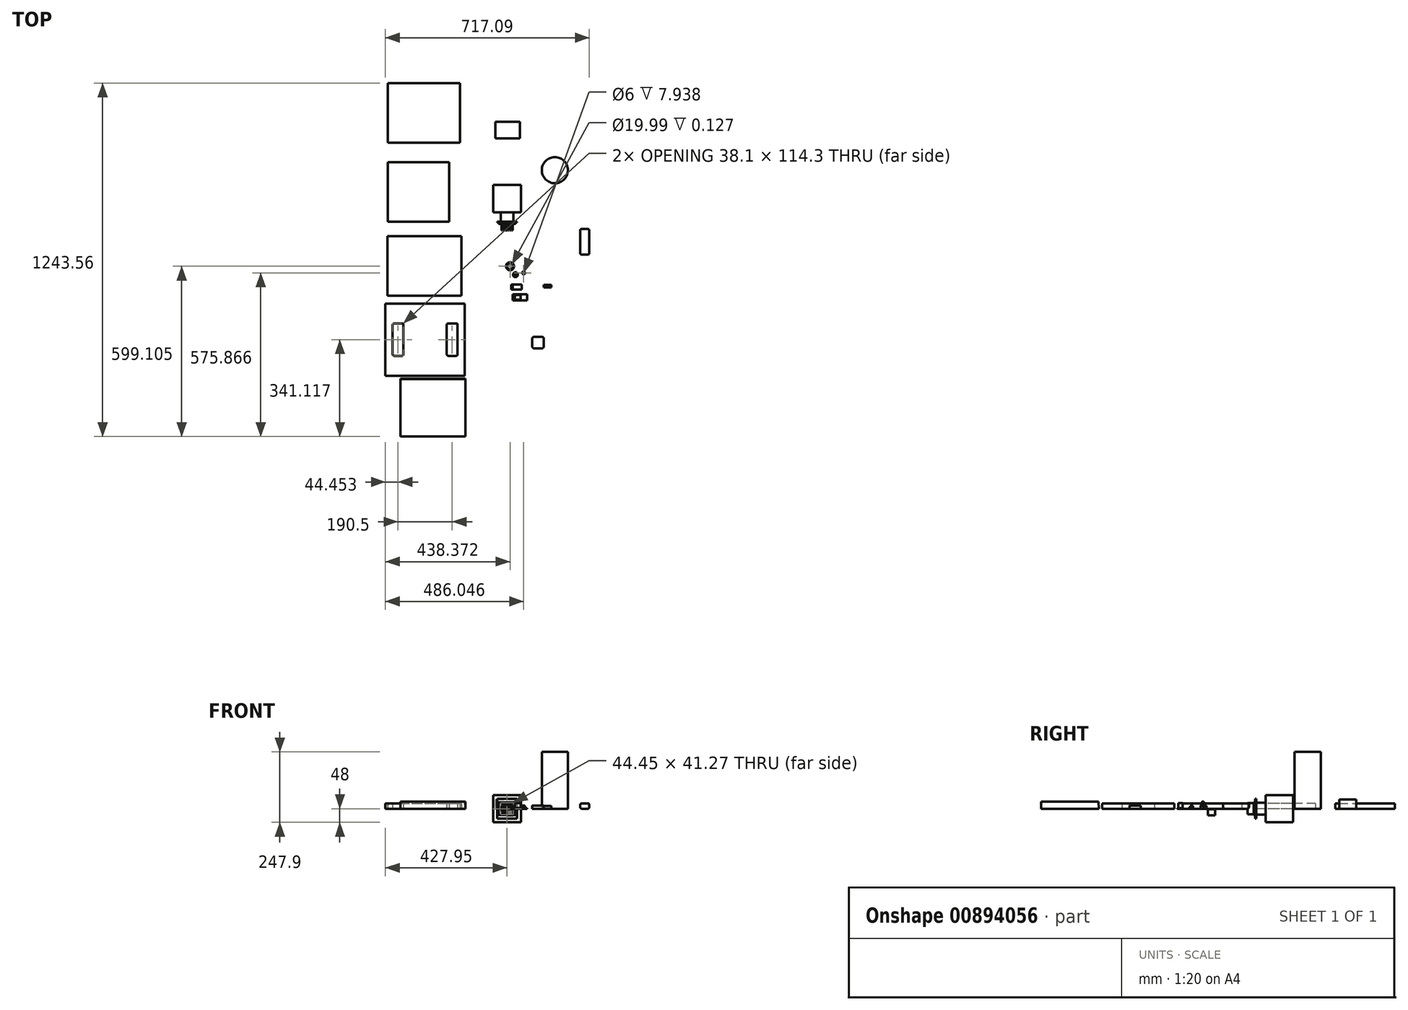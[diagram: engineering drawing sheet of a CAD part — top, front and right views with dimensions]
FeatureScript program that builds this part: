
annotation { "Feature Type Name" : "Feature", "Feature Type Description" : "" }
export const myFeature = defineFeature(function(context is Context, id is Id, definition is map)
    precondition{}
    {
        {
            var Q0;
            Q0=qCreatedBy(makeId("Front.planeOp"),FACE);
            var sketch = newSketch(context, id + "F0", { "sketchPlane" : qUnion([Q0])});
            skLineSegment(sketch, "E0.bottom", {"start": v(49, 48) * mm, "end": v(-49, 48) * mm});
            skLineSegment(sketch, "E0.top", {"start": v(49, -48) * mm, "end": v(-49, -48) * mm});
            skLineSegment(sketch, "E0.left", {"start": v(49, 48) * mm, "end": v(49, -48) * mm});
            skLineSegment(sketch, "E0.right", {"start": v(-49, 48) * mm, "end": v(-49, -48) * mm});
            skPoint(sketch, "E0.middle", {"position": v(0, 0) * mm});
            skSolve(sketch);
        }
        {
            var Q0;
            Q0 = qSketchRegion(id + "F0", true);
            extrude(context, id + "F1", {"entities" : qUnion([Q0]), "endBound" : BoundingType.SYMMETRIC, "depth" : 96.52 * mm, "offsetDistance" : 25.4 * mm});
        }
        {
            var Q0;
            Q0=qCreatedBy(makeId("Top.planeOp"),FACE);
            var sketch = newSketch(context, id + "F2", { "sketchPlane" : qUnion([Q0])});
            skLineSegment(sketch, "E1.bottom", {"start": v(-41.13, 211.34) * mm, "end": v(44.87, 211.34) * mm});
            skLineSegment(sketch, "E1.top", {"start": v(-41.13, 270.34) * mm, "end": v(44.87, 270.34) * mm});
            skLineSegment(sketch, "E1.left", {"start": v(-41.13, 211.34) * mm, "end": v(-41.13, 270.34) * mm});
            skLineSegment(sketch, "E1.right", {"start": v(44.87, 211.34) * mm, "end": v(44.87, 270.34) * mm});
            skSolve(sketch);
        }
        {
            var Q0;
            Q0 = qSketchRegion(id + "F2", true);
            extrude(context, id + "F3", {"entities" : qUnion([Q0]), "depth" : 33 * mm, "offsetDistance" : 25.4 * mm});
        }
        {
            var Q0;
            Q0=qCreatedBy(makeId("Top.planeOp"),FACE);
            var sketch = newSketch(context, id + "F4", { "sketchPlane" : qUnion([Q0])});
            skLineSegment(sketch, "E2.bottom", {"start": v(-419.23, 127.47) * mm, "end": v(-203.33, 127.47) * mm});
            skLineSegment(sketch, "E2.top", {"start": v(-419.23, -82.08) * mm, "end": v(-203.33, -82.08) * mm});
            skLineSegment(sketch, "E2.left", {"start": v(-419.23, 127.47) * mm, "end": v(-419.23, -82.08) * mm});
            skLineSegment(sketch, "E2.right", {"start": v(-203.33, 127.47) * mm, "end": v(-203.33, -82.08) * mm});
            skLineSegment(sketch, "E3.bottom", {"start": v(-420.68, -132.1) * mm, "end": v(-160.33, -132.1) * mm});
            skLineSegment(sketch, "E3.top", {"start": v(-420.68, -341.65) * mm, "end": v(-160.33, -341.65) * mm});
            skLineSegment(sketch, "E3.left", {"start": v(-420.68, -132.1) * mm, "end": v(-420.68, -341.65) * mm});
            skLineSegment(sketch, "E3.right", {"start": v(-160.33, -132.1) * mm, "end": v(-160.33, -341.65) * mm});
            skLineSegment(sketch, "E4.bottom", {"start": v(-427.95, -369.22) * mm, "end": v(-148.55, -369.22) * mm});
            skLineSegment(sketch, "E4.top", {"start": v(-427.95, -623.22) * mm, "end": v(-148.55, -623.22) * mm});
            skLineSegment(sketch, "E4.left", {"start": v(-427.95, -369.22) * mm, "end": v(-427.95, -623.22) * mm});
            skLineSegment(sketch, "E4.right", {"start": v(-148.55, -369.22) * mm, "end": v(-148.55, -623.22) * mm});
            skLineSegment(sketch, "E5.bottom", {"start": v(-212.05, -439.07) * mm, "end": v(-173.95, -439.07) * mm});
            skLineSegment(sketch, "E5.top", {"start": v(-212.05, -553.37) * mm, "end": v(-173.95, -553.37) * mm});
            skLineSegment(sketch, "E5.left", {"start": v(-212.05, -439.07) * mm, "end": v(-212.05, -553.37) * mm});
            skLineSegment(sketch, "E5.right", {"start": v(-173.95, -439.07) * mm, "end": v(-173.95, -553.37) * mm});
            skLineSegment(sketch, "E6", {"start": v(-427.95, -496.22) * mm, "end": v(-148.55, -496.22) * mm, "construction": true});
            skPoint(sketch, "E7", {"position": v(-173.95, -496.22) * mm});
            skLineSegment(sketch, "E8.bottom", {"start": v(-364.45, -439.07) * mm, "end": v(-402.55, -439.07) * mm});
            skLineSegment(sketch, "E8.top", {"start": v(-364.45, -553.37) * mm, "end": v(-402.55, -553.37) * mm});
            skLineSegment(sketch, "E8.left", {"start": v(-364.45, -439.07) * mm, "end": v(-364.45, -553.37) * mm});
            skLineSegment(sketch, "E8.right", {"start": v(-402.55, -439.07) * mm, "end": v(-402.55, -553.37) * mm});
            skPoint(sketch, "E8.middle", {"position": v(-383.5, -496.22) * mm});
            skLineSegment(sketch, "E9.bottom", {"start": v(-419.23, 196.67) * mm, "end": v(-165.23, 196.67) * mm});
            skLineSegment(sketch, "E9.top", {"start": v(-419.23, 406.22) * mm, "end": v(-165.23, 406.22) * mm});
            skLineSegment(sketch, "E9.left", {"start": v(-419.23, 196.67) * mm, "end": v(-419.23, 406.22) * mm});
            skLineSegment(sketch, "E9.right", {"start": v(-165.23, 196.67) * mm, "end": v(-165.23, 406.22) * mm});
            skSolve(sketch);
        }
        {
            var Q0;
            Q0=qCreatedBy(makeId("Top.planeOp"),FACE);
            var sketch = newSketch(context, id + "F5", { "sketchPlane" : qUnion([Q0])});
            skCircle(sketch, "E10", {"center": v(168.13, 99.9) * mm, "radius": 45.97 * mm});
            skSolve(sketch);
        }
        {
            var Q0;
            Q0 = qSketchRegion(id + "F5", true);
            extrude(context, id + "F6", {"entities" : qUnion([Q0]), "depth" : 199.9 * mm, "offsetDistance" : 25.4 * mm});
        }
        {
            var Q0;
            Q0=makeQuery(id+"F4.imprint","IMPRINT",FACE,{"disambiguationData":[TD([[makeQuery(id+"F4.imprint","IMPRINT",EDGE,{"derivedFrom":sQuery(id+"F4.wireOp",EDGE,"E4.bottom")}),-1.0]])]});
            var Q1;
            Q1=makeQuery(id+"F4.imprint","IMPRINT",FACE,{"disambiguationData":[TD([[makeQuery(id+"F4.imprint","IMPRINT",EDGE,{"derivedFrom":sQuery(id+"F4.wireOp",EDGE,"E3.bottom")}),-1.0]])]});
            var Q2;
            Q2=makeQuery(id+"F4.imprint","IMPRINT",FACE,{"disambiguationData":[TD([[makeQuery(id+"F4.imprint","IMPRINT",EDGE,{"derivedFrom":sQuery(id+"F4.wireOp",EDGE,"E2.bottom")}),-1.0]])]});
            var Q3;
            Q3=makeQuery(id+"F4.imprint","IMPRINT",FACE,{"disambiguationData":[TD([[makeQuery(id+"F4.imprint","IMPRINT",EDGE,{"derivedFrom":sQuery(id+"F4.wireOp",EDGE,"E9.bottom")}),1.0]])]});
            extrude(context, id + "F7", {"entities" : qUnion([Q0, Q1, Q2, Q3]), "depth" : 19.05 * mm, "offsetDistance" : 25.4 * mm});
        }
        {
            var Q0;
            Q0=makeQuery(id+"F1.opExtrude","CAP_FACE",FACE,{"disambiguationData":[OSD([sQuery(id+"F0.wireOp",EDGE,"E0.bottom"),sQuery(id+"F0.wireOp",EDGE,"E0.top"),sQuery(id+"F0.wireOp",EDGE,"E0.left"),sQuery(id+"F0.wireOp",EDGE,"E0.right")])],"isStart":false});
            var sketch = newSketch(context, id + "F8", { "sketchPlane" : qUnion([Q0])});
            skLineSegment(sketch, "E11.bottom", {"start": v(22.23, 20.64) * mm, "end": v(-22.23, 20.64) * mm});
            skLineSegment(sketch, "E11.top", {"start": v(22.22, -20.64) * mm, "end": v(-22.22, -20.64) * mm});
            skLineSegment(sketch, "E11.left", {"start": v(22.23, 20.64) * mm, "end": v(22.23, -20.64) * mm});
            skLineSegment(sketch, "E11.right", {"start": v(-22.23, 20.64) * mm, "end": v(-22.23, -20.64) * mm});
            skPoint(sketch, "E11.middle", {"position": v(0, 0) * mm});
            skSolve(sketch);
        }
        {
            var Q0;
            Q0 = qSketchRegion(id + "F8", true);
            extrude(context, id + "F9", {"entities" : qUnion([Q0]), "operationType" : NewBodyOperationType.ADD, "depth" : 33.02 * mm, "offsetDistance" : 25.4 * mm});
        }
        {
            var Q0;
            Q0=makeQuery(id+"F9.opExtrude","CAP_FACE",FACE,{"disambiguationData":[OSD([sQuery(id+"F8.wireOp",EDGE,"E11.bottom"),sQuery(id+"F8.wireOp",EDGE,"E11.top"),sQuery(id+"F8.wireOp",EDGE,"E11.left"),sQuery(id+"F8.wireOp",EDGE,"E11.right")])],"isStart":false});
            var sketch = newSketch(context, id + "F10", { "sketchPlane" : qUnion([Q0])});
            skLineSegment(sketch, "E12.bottom", {"start": v(34.92, 34.93) * mm, "end": v(-34.93, 34.93) * mm});
            skLineSegment(sketch, "E12.top", {"start": v(34.93, -34.93) * mm, "end": v(-34.92, -34.93) * mm});
            skLineSegment(sketch, "E12.left", {"start": v(34.92, 34.93) * mm, "end": v(34.93, -34.93) * mm});
            skLineSegment(sketch, "E12.right", {"start": v(-34.93, 34.93) * mm, "end": v(-34.92, -34.93) * mm});
            skPoint(sketch, "E12.middle", {"position": v(0, 0) * mm});
            skSolve(sketch);
        }
        {
            var Q0;
            Q0 = qSketchRegion(id + "F10", true);
            extrude(context, id + "F11", {"entities" : qUnion([Q0]), "operationType" : NewBodyOperationType.ADD, "depth" : 3.3 * mm, "offsetDistance" : 25.4 * mm});
        }
        {
            var Q0;
            Q0=makeQuery(id+"F11.opExtrude","CAP_FACE",FACE,{"disambiguationData":[OSD([sQuery(id+"F10.wireOp",EDGE,"E12.bottom"),sQuery(id+"F10.wireOp",EDGE,"E12.top"),sQuery(id+"F10.wireOp",EDGE,"E12.left"),sQuery(id+"F10.wireOp",EDGE,"E12.right")])],"isStart":false});
            var sketch = newSketch(context, id + "F12", { "sketchPlane" : qUnion([Q0])});
            skLineSegment(sketch, "E13.bottom", {"start": v(30.23, 22.5) * mm, "end": v(-30.23, 22.5) * mm});
            skLineSegment(sketch, "E13.top", {"start": v(30.23, -22.5) * mm, "end": v(-30.23, -22.5) * mm});
            skLineSegment(sketch, "E13.left", {"start": v(30.23, 22.5) * mm, "end": v(30.23, -22.5) * mm});
            skLineSegment(sketch, "E13.right", {"start": v(-30.23, 22.5) * mm, "end": v(-30.23, -22.5) * mm});
            skPoint(sketch, "E13.middle", {"position": v(0, 0) * mm});
            skSolve(sketch);
        }
        {
            var Q0;
            Q0 = qSketchRegion(id + "F12", true);
            extrude(context, id + "F13", {"entities" : qUnion([Q0]), "operationType" : NewBodyOperationType.ADD, "depth" : 4.76 * mm, "offsetDistance" : 25.4 * mm});
        }
        {
            var Q0;
            Q0=makeQuery(id+"F13.opExtrude","CAP_FACE",FACE,{"disambiguationData":[OSD([sQuery(id+"F12.wireOp",EDGE,"E13.bottom"),sQuery(id+"F12.wireOp",EDGE,"E13.top"),sQuery(id+"F12.wireOp",EDGE,"E13.left"),sQuery(id+"F12.wireOp",EDGE,"E13.right")])],"isStart":false});
            var sketch = newSketch(context, id + "F14", { "sketchPlane" : qUnion([Q0])});
            skLineSegment(sketch, "E14.bottom", {"start": v(19.84, 19.84) * mm, "end": v(-19.84, 19.84) * mm});
            skLineSegment(sketch, "E14.top", {"start": v(19.84, -19.84) * mm, "end": v(-19.84, -19.84) * mm});
            skLineSegment(sketch, "E14.left", {"start": v(19.84, 19.84) * mm, "end": v(19.84, -19.84) * mm});
            skLineSegment(sketch, "E14.right", {"start": v(-19.84, 19.84) * mm, "end": v(-19.84, -19.84) * mm});
            skPoint(sketch, "E14.middle", {"position": v(0, 0) * mm});
            skLineSegment(sketch, "E15", {"start": v(-17.3, 19.84) * mm, "end": v(-17.3, -19.84) * mm});
            skLineSegment(sketch, "E16.1.0.0", {"start": v(-15.02, 19.84) * mm, "end": v(-15.02, -19.84) * mm});
            skLineSegment(sketch, "E16.2.0.0", {"start": v(-12.73, 19.84) * mm, "end": v(-12.73, -19.84) * mm});
            skLineSegment(sketch, "E16.3.0.0", {"start": v(-10.45, 19.84) * mm, "end": v(-10.45, -19.84) * mm});
            skLineSegment(sketch, "E16.4.0.0", {"start": v(-8.16, 19.84) * mm, "end": v(-8.16, -19.84) * mm});
            skLineSegment(sketch, "E16.5.0.0", {"start": v(-5.87, 19.84) * mm, "end": v(-5.87, -19.84) * mm});
            skLineSegment(sketch, "E16.6.0.0", {"start": v(-3.59, 19.84) * mm, "end": v(-3.59, -19.84) * mm});
            skLineSegment(sketch, "E16.7.0.0", {"start": v(-1.3, 19.84) * mm, "end": v(-1.3, -19.84) * mm});
            skLineSegment(sketch, "E16.8.0.0", {"start": v(0.98, 19.84) * mm, "end": v(0.98, -19.84) * mm});
            skLineSegment(sketch, "E16.9.0.0", {"start": v(3.27, 19.84) * mm, "end": v(3.27, -19.84) * mm});
            skLineSegment(sketch, "E16.10.0.0", {"start": v(5.56, 19.84) * mm, "end": v(5.56, -19.84) * mm});
            skLineSegment(sketch, "E16.11.0.0", {"start": v(7.84, 19.84) * mm, "end": v(7.84, -19.84) * mm});
            skLineSegment(sketch, "E16.12.0.0", {"start": v(10.13, 19.84) * mm, "end": v(10.13, -19.84) * mm});
            skLineSegment(sketch, "E16.13.0.0", {"start": v(12.41, 19.84) * mm, "end": v(12.41, -19.84) * mm});
            skLineSegment(sketch, "E16.14.0.0", {"start": v(14.7, 19.84) * mm, "end": v(14.7, -19.84) * mm});
            skLineSegment(sketch, "E16.direction1", {"start": v(-17.3, -19.84) * mm, "end": v(-15.02, -19.84) * mm, "construction": true});
            skLineSegment(sketch, "E17.0.15.0", {"start": v(16.99, 19.84) * mm, "end": v(16.99, -19.84) * mm});
            skSolve(sketch);
        }
        {
            var Q0;
            {var subQ0=sQuery(id+"F14.wireOp",EDGE,"E14.right");Q0=makeQuery(id+"F14.imprint","IMPRINT",FACE,{"disambiguationData":[TD([[makeQuery(id+"F14.imprint","IMPRINT",EDGE,{"derivedFrom":subQ0}),1.0]])]});}
            var Q1;
            {var subQ0=sQuery(id+"F14.wireOp",EDGE,"E16.1.0.0");Q1=makeQuery(id+"F14.imprint","IMPRINT",FACE,{"disambiguationData":[TD([[makeQuery(id+"F14.imprint","IMPRINT",EDGE,{"derivedFrom":subQ0}),1.0]])]});}
            var Q2;
            {var subQ0=sQuery(id+"F14.wireOp",EDGE,"E16.3.0.0");Q2=makeQuery(id+"F14.imprint","IMPRINT",FACE,{"disambiguationData":[TD([[makeQuery(id+"F14.imprint","IMPRINT",EDGE,{"derivedFrom":subQ0}),1.0]])]});}
            var Q3;
            {var subQ0=sQuery(id+"F14.wireOp",EDGE,"E16.5.0.0");Q3=makeQuery(id+"F14.imprint","IMPRINT",FACE,{"disambiguationData":[TD([[makeQuery(id+"F14.imprint","IMPRINT",EDGE,{"derivedFrom":subQ0}),1.0]])]});}
            var Q4;
            {var subQ0=sQuery(id+"F14.wireOp",EDGE,"E16.7.0.0");Q4=makeQuery(id+"F14.imprint","IMPRINT",FACE,{"disambiguationData":[TD([[makeQuery(id+"F14.imprint","IMPRINT",EDGE,{"derivedFrom":subQ0}),1.0]])]});}
            var Q5;
            {var subQ0=sQuery(id+"F14.wireOp",EDGE,"E16.9.0.0");Q5=makeQuery(id+"F14.imprint","IMPRINT",FACE,{"disambiguationData":[TD([[makeQuery(id+"F14.imprint","IMPRINT",EDGE,{"derivedFrom":subQ0}),1.0]])]});}
            var Q6;
            {var subQ0=sQuery(id+"F14.wireOp",EDGE,"E16.11.0.0");Q6=makeQuery(id+"F14.imprint","IMPRINT",FACE,{"disambiguationData":[TD([[makeQuery(id+"F14.imprint","IMPRINT",EDGE,{"derivedFrom":subQ0}),1.0]])]});}
            var Q7;
            {var subQ0=sQuery(id+"F14.wireOp",EDGE,"E16.13.0.0");Q7=makeQuery(id+"F14.imprint","IMPRINT",FACE,{"disambiguationData":[TD([[makeQuery(id+"F14.imprint","IMPRINT",EDGE,{"derivedFrom":subQ0}),1.0]])]});}
            var Q8;
            {var subQ0=sQuery(id+"F14.wireOp",EDGE,"E14.left");Q8=makeQuery(id+"F14.imprint","IMPRINT",FACE,{"disambiguationData":[TD([[makeQuery(id+"F14.imprint","IMPRINT",EDGE,{"derivedFrom":subQ0}),-1.0]])]});}
            extrude(context, id + "F15", {"entities" : qUnion([Q0, Q1, Q2, Q3, Q4, Q5, Q6, Q7, Q8]), "operationType" : NewBodyOperationType.ADD, "depth" : 22.22 * mm, "offsetDistance" : 25.4 * mm});
        }
        {
            var Q0;
            Q0=qCreatedBy(makeId("Top.planeOp"),FACE);
            var sketch = newSketch(context, id + "F16", { "sketchPlane" : qUnion([Q0])});
            skLineSegment(sketch, "E18.bottom", {"start": v(257.4, -106.84) * mm, "end": v(289.14, -106.84) * mm});
            skLineSegment(sketch, "E18.top", {"start": v(257.4, -197.32) * mm, "end": v(289.14, -197.32) * mm});
            skLineSegment(sketch, "E18.left", {"start": v(257.4, -106.84) * mm, "end": v(257.4, -197.32) * mm});
            skLineSegment(sketch, "E18.right", {"start": v(289.14, -106.84) * mm, "end": v(289.14, -197.32) * mm});
            skSolve(sketch);
        }
        {
            var Q0;
            Q0 = qSketchRegion(id + "F16", true);
            extrude(context, id + "F17", {"entities" : qUnion([Q0]), "depth" : 19.05 * mm, "offsetDistance" : 25.4 * mm});
        }
        {
            var Q0;
            Q0=makeQuery(id+"F17.opExtrude","CAP_FACE",FACE,{"disambiguationData":[OSD([sQuery(id+"F16.wireOp",EDGE,"E18.bottom"),sQuery(id+"F16.wireOp",EDGE,"E18.top"),sQuery(id+"F16.wireOp",EDGE,"E18.left"),sQuery(id+"F16.wireOp",EDGE,"E18.right")])],"isStart":false});
            var Q1;
            Q1=makeQuery(id+"F17.opExtrude","SWEPT_FACE",FACE,{"disambiguationData":[OSD([sQuery(id+"F16.wireOp",EDGE,"E18.top")])]});
            var Q2;
            Q2=makeQuery(id+"F17.opExtrude","SWEPT_FACE",FACE,{"disambiguationData":[OSD([sQuery(id+"F16.wireOp",EDGE,"E18.bottom")])]});
            var Q3;
            Q3=makeQuery(id+"F17.opExtrude","CAP_FACE",FACE,{"disambiguationData":[OSD([sQuery(id+"F16.wireOp",EDGE,"E18.bottom"),sQuery(id+"F16.wireOp",EDGE,"E18.top"),sQuery(id+"F16.wireOp",EDGE,"E18.left"),sQuery(id+"F16.wireOp",EDGE,"E18.right")])],"isStart":true});
            fillet(context, id + "F18", {"entities" : qUnion([Q0, Q1, Q2, Q3]), "radius" : 5.08 * mm, "tangentPropagation" : true, "allowEdgeOverflow" : false});
        }
        {
            var Q0;
            Q0=qCreatedBy(makeId("Top.planeOp"),FACE);
            var sketch = newSketch(context, id + "F19", { "sketchPlane" : qUnion([Q0])});
            skLineSegment(sketch, "E19.bottom", {"start": v(-374.6, -634.14) * mm, "end": v(-146, -634.14) * mm});
            skLineSegment(sketch, "E19.top", {"start": v(-374.6, -837.34) * mm, "end": v(-146, -837.34) * mm});
            skLineSegment(sketch, "E19.left", {"start": v(-374.6, -634.14) * mm, "end": v(-374.6, -837.34) * mm});
            skLineSegment(sketch, "E19.right", {"start": v(-146, -634.14) * mm, "end": v(-146, -837.34) * mm});
            skSolve(sketch);
        }
        {
            var Q0;
            Q0=makeQuery(id+"F19.imprint","IMPRINT",FACE,{"disambiguationData":[TD([[makeQuery(id+"F19.imprint","IMPRINT",EDGE,{"derivedFrom":sQuery(id+"F19.wireOp",EDGE,"E19.bottom")}),-1.0]])]});
            extrude(context, id + "F20", {"entities" : qUnion([Q0]), "depth" : 25.4 * mm, "offsetDistance" : 25.4 * mm});
        }
        {
            var Q0;
            Q0=makeQuery(id+"F20.opExtrude","SWEPT_FACE",FACE,{"disambiguationData":[OSD([sQuery(id+"F19.wireOp",EDGE,"E19.left")])]});
            var sketch = newSketch(context, id + "F21", { "sketchPlane" : qUnion([Q0])});
            skCircle(sketch, "E20", {"center": v(862.74, 0) * mm, "radius": 228.6 * mm, "construction": true});
            skPoint(sketch, "E21", {"position": v(634.14, 0) * mm});
            skPoint(sketch, "E22", {"position": v(635.56, 25.4) * mm});
            skLineSegment(sketch, "E23", {"start": v(634.14, 0) * mm, "end": v(635.56, 25.4) * mm});
            skLineSegment(sketch, "E24", {"start": v(635.56, 25.4) * mm, "end": v(634.14, 25.4) * mm});
            skLineSegment(sketch, "E25", {"start": v(634.14, 25.4) * mm, "end": v(634.14, 0) * mm});
            skSolve(sketch);
        }
        {
            var Q0;
            Q0 = qSketchRegion(id + "F21", true);
            extrude(context, id + "F22", {"entities" : qUnion([Q0]), "operationType" : NewBodyOperationType.REMOVE, "endBound" : BoundingType.THROUGH_ALL, "oppositeDirection" : true, "depth" : 25.4 * mm, "offsetDistance" : 25.4 * mm});
        }
        {
            var Q0;
            Q0=qCreatedBy(makeId("Top.planeOp"),FACE);
            var sketch = newSketch(context, id + "F23", { "sketchPlane" : qUnion([Q0])});
            skLineSegment(sketch, "E26.bottom", {"start": v(14.78, -319.9) * mm, "end": v(51.3, -319.9) * mm});
            skLineSegment(sketch, "E26.top", {"start": v(14.78, -302.43) * mm, "end": v(51.3, -302.43) * mm});
            skLineSegment(sketch, "E26.left", {"start": v(14.78, -319.9) * mm, "end": v(14.78, -302.43) * mm});
            skLineSegment(sketch, "E26.right", {"start": v(51.3, -319.9) * mm, "end": v(51.3, -302.43) * mm});
            skSolve(sketch);
        }
        {
            var Q0;
            Q0 = qSketchRegion(id + "F23", true);
            extrude(context, id + "F24", {"entities" : qUnion([Q0]), "depth" : 1.59 * mm, "offsetDistance" : 25.4 * mm});
        }
        {
            var Q0;
            Q0=makeQuery(id+"F24.opExtrude","CAP_FACE",FACE,{"disambiguationData":[OSD([sQuery(id+"F23.wireOp",EDGE,"E26.bottom"),sQuery(id+"F23.wireOp",EDGE,"E26.top"),sQuery(id+"F23.wireOp",EDGE,"E26.left"),sQuery(id+"F23.wireOp",EDGE,"E26.right")])],"isStart":false});
            var sketch = newSketch(context, id + "F25", { "sketchPlane" : qUnion([Q0])});
            skLineSegment(sketch, "E27.bottom", {"start": v(14.78, -307.2) * mm, "end": v(19.54, -307.2) * mm});
            skLineSegment(sketch, "E27.top", {"start": v(14.78, -315.13) * mm, "end": v(19.54, -315.13) * mm});
            skLineSegment(sketch, "E27.left", {"start": v(14.78, -307.2) * mm, "end": v(14.78, -315.13) * mm});
            skLineSegment(sketch, "E27.right", {"start": v(19.54, -307.2) * mm, "end": v(19.54, -315.13) * mm});
            skLineSegment(sketch, "E28", {"start": v(51.3, -311.16) * mm, "end": v(14.78, -311.16) * mm, "construction": true});
            skSolve(sketch);
        }
        {
            var Q0;
            Q0 = qSketchRegion(id + "F25", true);
            extrude(context, id + "F26", {"entities" : qUnion([Q0]), "operationType" : NewBodyOperationType.ADD, "depth" : 1.59 * mm, "offsetDistance" : 25.4 * mm});
        }
        {
            var Q0;
            Q0=qCreatedBy(makeId("Top.planeOp"),FACE);
            var sketch = newSketch(context, id + "F27", { "sketchPlane" : qUnion([Q0])});
            skLineSegment(sketch, "E29.bottom", {"start": v(19.61, -336.6) * mm, "end": v(70.41, -336.6) * mm});
            skLineSegment(sketch, "E29.top", {"start": v(19.61, -358.82) * mm, "end": v(70.41, -358.82) * mm});
            skLineSegment(sketch, "E29.left", {"start": v(19.61, -336.6) * mm, "end": v(19.61, -358.82) * mm});
            skLineSegment(sketch, "E29.right", {"start": v(70.41, -336.6) * mm, "end": v(70.41, -358.82) * mm});
            skSolve(sketch);
        }
        {
            var Q0;
            Q0 = qSketchRegion(id + "F27", true);
            extrude(context, id + "F28", {"entities" : qUnion([Q0]), "depth" : 1.59 * mm, "offsetDistance" : 25.4 * mm});
        }
        {
            var Q0;
            Q0=makeQuery(id+"F28.opExtrude","CAP_FACE",FACE,{"disambiguationData":[OSD([sQuery(id+"F27.wireOp",EDGE,"E29.bottom"),sQuery(id+"F27.wireOp",EDGE,"E29.top"),sQuery(id+"F27.wireOp",EDGE,"E29.left"),sQuery(id+"F27.wireOp",EDGE,"E29.right")])],"isStart":false});
            var sketch = newSketch(context, id + "F29", { "sketchPlane" : qUnion([Q0])});
            skLineSegment(sketch, "E30", {"start": v(19.61, -347.7) * mm, "end": v(70.41, -347.7) * mm, "construction": true});
            skLineSegment(sketch, "E31.bottom", {"start": v(48.19, -355.64) * mm, "end": v(27.55, -355.64) * mm});
            skLineSegment(sketch, "E31.top", {"start": v(48.19, -339.77) * mm, "end": v(27.55, -339.77) * mm});
            skLineSegment(sketch, "E31.left", {"start": v(48.19, -355.64) * mm, "end": v(48.19, -339.77) * mm});
            skLineSegment(sketch, "E31.right", {"start": v(27.55, -355.64) * mm, "end": v(27.55, -339.77) * mm});
            skPoint(sketch, "E31.middle", {"position": v(37.87, -347.7) * mm});
            skSolve(sketch);
        }
        {
            var Q0;
            Q0 = qSketchRegion(id + "F29", true);
            extrude(context, id + "F30", {"entities" : qUnion([Q0]), "operationType" : NewBodyOperationType.ADD, "depth" : 18.26 * mm, "offsetDistance" : 25.4 * mm});
        }
        {
            var Q0;
            Q0=qCreatedBy(makeId("Top.planeOp"),FACE);
            var sketch = newSketch(context, id + "F31", { "sketchPlane" : qUnion([Q0])});
            skCircle(sketch, "E32", {"center": v(29.51, -267.96) * mm, "radius": 8.5 * mm});
            skSolve(sketch);
        }
        {
            var Q0;
            Q0 = qSketchRegion(id + "F31", true);
            extrude(context, id + "F32", {"entities" : qUnion([Q0]), "depth" : 9.5 * mm, "offsetDistance" : 25.4 * mm});
        }
        {
            var Q0;
            Q0=makeQuery(id+"F32.opExtrude","CAP_FACE",FACE,{"disambiguationData":[OSD([sQuery(id+"F31.wireOp",EDGE,"E32")])],"isStart":false});
            var sketch = newSketch(context, id + "F33", { "sketchPlane" : qUnion([Q0])});
            skLineSegment(sketch, "E33", {"start": v(29.51, -276.46) * mm, "end": v(29.51, -259.46) * mm, "construction": true});
            skPoint(sketch, "E34", {"position": v(29.51, -267.96) * mm});
            skLineSegment(sketch, "E35", {"start": v(21.01, -267.96) * mm, "end": v(38.01, -267.96) * mm, "construction": true});
            skLineSegment(sketch, "E36.bottom", {"start": v(28.11, -276.36) * mm, "end": v(30.91, -276.36) * mm, "construction": true});
            skLineSegment(sketch, "E36.top", {"start": v(28.11, -275.16) * mm, "end": v(30.91, -275.16) * mm, "construction": true});
            skLineSegment(sketch, "E36.left", {"start": v(28.11, -276.36) * mm, "end": v(28.11, -275.16) * mm, "construction": true});
            skLineSegment(sketch, "E36.right", {"start": v(30.91, -276.36) * mm, "end": v(30.91, -275.16) * mm, "construction": true});
            skArc(sketch, "E37", {"start": v(28.71, -275.16) * mm, "mid": v(28.11, -275.76) * mm, "end": v(28.71, -276.36) * mm});
            skPoint(sketch, "E37.centerSnap0", {"position": v(28.11, -275.76) * mm});
            skArc(sketch, "E38", {"start": v(30.31, -276.36) * mm, "mid": v(30.91, -275.76) * mm, "end": v(30.31, -275.16) * mm});
            skPoint(sketch, "E38.centerSnap0", {"position": v(30.91, -275.76) * mm});
            skLineSegment(sketch, "E39", {"start": v(28.71, -275.16) * mm, "end": v(30.31, -275.16) * mm});
            skLineSegment(sketch, "E40", {"start": v(28.71, -276.36) * mm, "end": v(30.31, -276.36) * mm});
            skPoint(sketch, "E41", {"position": v(29.51, -276.36) * mm});
            skCircle(sketch, "E42", {"center": v(29.51, -267.96) * mm, "radius": 3 * mm});
            skSolve(sketch);
        }
        {
            var Q0;
            Q0=makeQuery(id+"F33.imprint","IMPRINT",FACE,{"disambiguationData":[TD([[makeQuery(id+"F33.imprint","IMPRINT",EDGE,{"derivedFrom":sQuery(id+"F33.wireOp",EDGE,"E37")}),1.0]])]});
            extrude(context, id + "F34", {"entities" : qUnion([Q0]), "operationType" : NewBodyOperationType.ADD, "depth" : 2 * mm, "offsetDistance" : 25.4 * mm});
        }
        {
            var Q0;
            Q0=makeQuery(id+"F33.imprint","IMPRINT",FACE,{"disambiguationData":[TD([[makeQuery(id+"F33.imprint","IMPRINT",EDGE,{"derivedFrom":sQuery(id+"F33.wireOp",EDGE,"E42")}),1.0]])]});
            extrude(context, id + "F35", {"entities" : qUnion([Q0]), "operationType" : NewBodyOperationType.ADD, "depth" : 15.5 * mm, "offsetDistance" : 25.4 * mm});
        }
        {
            var Q0;
            Q0=qCreatedBy(makeId("Top.planeOp"),FACE);
            var sketch = newSketch(context, id + "F36", { "sketchPlane" : qUnion([Q0])});
            skCircle(sketch, "E43", {"center": v(58.1, -261.47) * mm, "radius": 5 * mm});
            skSolve(sketch);
        }
        {
            var Q0;
            Q0 = qSketchRegion(id + "F36", true);
            extrude(context, id + "F37", {"entities" : qUnion([Q0]), "depth" : 11.1 * mm, "offsetDistance" : 25.4 * mm});
        }
        {
            var Q0;
            Q0=makeQuery(id+"F37.opExtrude","CAP_FACE",FACE,{"disambiguationData":[OSD([sQuery(id+"F36.wireOp",EDGE,"E43")])],"isStart":true});
            var sketch = newSketch(context, id + "F38", { "sketchPlane" : qUnion([Q0])});
            skPoint(sketch, "E44", {"position": v(58.1, 261.47) * mm});
            skCircle(sketch, "E45", {"center": v(58.1, 261.47) * mm, "radius": 3 * mm});
            skSolve(sketch);
        }
        {
            var Q0;
            Q0 = qSketchRegion(id + "F38", true);
            extrude(context, id + "F39", {"entities" : qUnion([Q0]), "operationType" : NewBodyOperationType.REMOVE, "oppositeDirection" : true, "depth" : 7.94 * mm, "offsetDistance" : 25.4 * mm});
        }
        {
            var Q0;
            Q0=qCreatedBy(makeId("Top.planeOp"),FACE);
            var sketch = newSketch(context, id + "F40", { "sketchPlane" : qUnion([Q0])});
            skCircle(sketch, "E46", {"center": v(10.42, -238.24) * mm, "radius": 13.96 * mm});
            skSolve(sketch);
        }
        {
            var Q0;
            Q0 = qSketchRegion(id + "F40", true);
            extrude(context, id + "F41", {"entities" : qUnion([Q0]), "oppositeDirection" : true, "depth" : 1.93 * mm, "offsetDistance" : 25.4 * mm});
        }
        {
            var Q0;
            Q0=makeQuery(id+"F41.opExtrude","CAP_FACE",FACE,{"disambiguationData":[OSD([sQuery(id+"F40.wireOp",EDGE,"E46")])],"isStart":false});
            var sketch = newSketch(context, id + "F42", { "sketchPlane" : qUnion([Q0])});
            skPoint(sketch, "E47", {"position": v(10.42, 238.24) * mm});
            skCircle(sketch, "E48", {"center": v(10.42, 238.24) * mm, "radius": 12.46 * mm});
            skSolve(sketch);
        }
        {
            var Q0;
            Q0 = qSketchRegion(id + "F42", true);
            extrude(context, id + "F43", {"entities" : qUnion([Q0]), "operationType" : NewBodyOperationType.ADD, "depth" : 21.54 * mm, "offsetDistance" : 25.4 * mm});
        }
        {
            var Q0;
            Q0=makeQuery(id+"F41.opExtrude","CAP_EDGE",EDGE,{"disambiguationData":[OSD([sQuery(id+"F40.wireOp",EDGE,"E46")])],"isStart":true});
            chamfer(context, id + "F44", {"entities" : qUnion([Q0]), "chamferType" : ChamferType.OFFSET_ANGLE, "width" : 2.67 * mm, "oppositeDirection" : false, "angle" : 33 * degree, "tangentPropagation" : true});
        }
        {
            var Q0;
            Q0=makeQuery(id+"F41.opExtrude","CAP_FACE",FACE,{"disambiguationData":[OSD([sQuery(id+"F40.wireOp",EDGE,"E46")])],"isStart":true});
            var sketch = newSketch(context, id + "F45", { "sketchPlane" : qUnion([Q0])});
            skPoint(sketch, "E49", {"position": v(10.42, -238.24) * mm});
            skCircle(sketch, "E50", {"center": v(10.42, -238.24) * mm, "radius": 10 * mm});
            skSolve(sketch);
        }
        {
            var Q0;
            Q0 = qSketchRegion(id + "F45", true);
            extrude(context, id + "F46", {"entities" : qUnion([Q0]), "operationType" : NewBodyOperationType.REMOVE, "oppositeDirection" : true, "depth" : 0.13 * mm, "offsetDistance" : 25.4 * mm});
        }
        {
            var Q0;
            Q0=qCreatedBy(makeId("Top.planeOp"),FACE);
            var sketch = newSketch(context, id + "F47", { "sketchPlane" : qUnion([Q0])});
            skLineSegment(sketch, "E51.bottom", {"start": v(128.65, -303.23) * mm, "end": v(155.65, -303.23) * mm});
            skLineSegment(sketch, "E51.top", {"start": v(128.65, -312.98) * mm, "end": v(155.65, -312.98) * mm});
            skLineSegment(sketch, "E51.left", {"start": v(128.65, -303.23) * mm, "end": v(128.65, -312.98) * mm});
            skLineSegment(sketch, "E51.right", {"start": v(155.65, -303.23) * mm, "end": v(155.65, -312.98) * mm});
            skSolve(sketch);
        }
        {
            var Q0;
            Q0 = qSketchRegion(id + "F47", true);
            extrude(context, id + "F48", {"entities" : qUnion([Q0]), "depth" : 9.58 * mm, "offsetDistance" : 25.4 * mm});
        }
        {
            var Q0;
            Q0=qCreatedBy(makeId("Top.planeOp"),FACE);
            var sketch = newSketch(context, id + "F49", { "sketchPlane" : qUnion([Q0])});
            skLineSegment(sketch, "E52.bottom", {"start": v(88.78, -486.78) * mm, "end": v(128.76, -486.78) * mm});
            skLineSegment(sketch, "E52.top", {"start": v(88.78, -526.76) * mm, "end": v(128.76, -526.76) * mm});
            skLineSegment(sketch, "E52.left", {"start": v(88.78, -486.78) * mm, "end": v(88.78, -526.76) * mm});
            skLineSegment(sketch, "E52.right", {"start": v(128.76, -486.78) * mm, "end": v(128.76, -526.76) * mm});
            skSolve(sketch);
        }
        {
            var Q0;
            Q0 = qSketchRegion(id + "F49", true);
            extrude(context, id + "F50", {"entities" : qUnion([Q0]), "depth" : 10.44 * mm, "offsetDistance" : 25.4 * mm});
        }
        {
            var Q0;
            Q0=makeQuery(id+"F50.opExtrude","SWEPT_EDGE",EDGE,{"disambiguationData":[OSD([sQuery(id+"F49.wireOp",EDGE,"E52.top"),sQuery(id+"F49.wireOp",EDGE,"E52.right")])]});
            var Q1;
            Q1=makeQuery(id+"F50.opExtrude","SWEPT_EDGE",EDGE,{"disambiguationData":[OSD([sQuery(id+"F49.wireOp",EDGE,"E52.bottom"),sQuery(id+"F49.wireOp",EDGE,"E52.right")])]});
            var Q2;
            Q2=makeQuery(id+"F50.opExtrude","SWEPT_EDGE",EDGE,{"disambiguationData":[OSD([sQuery(id+"F49.wireOp",EDGE,"E52.top"),sQuery(id+"F49.wireOp",EDGE,"E52.left")])]});
            var Q3;
            Q3=makeQuery(id+"F50.opExtrude","SWEPT_EDGE",EDGE,{"disambiguationData":[OSD([sQuery(id+"F49.wireOp",EDGE,"E52.bottom"),sQuery(id+"F49.wireOp",EDGE,"E52.left")])]});
            fillet(context, id + "F51", {"entities" : qUnion([Q0, Q1, Q2, Q3]), "radius" : 5.08 * mm, "tangentPropagation" : true, "allowEdgeOverflow" : false});
        }
        {
            var Q0;
            Q0=makeQuery(id+"F7.opExtrude","SWEPT_EDGE",EDGE,{"disambiguationData":[OSD([sQuery(id+"F4.wireOp",EDGE,"E8.bottom"),sQuery(id+"F4.wireOp",EDGE,"E8.right")])]});
            var Q1;
            Q1=makeQuery(id+"F7.opExtrude","SWEPT_EDGE",EDGE,{"disambiguationData":[OSD([sQuery(id+"F4.wireOp",EDGE,"E8.bottom"),sQuery(id+"F4.wireOp",EDGE,"E8.left")])]});
            var Q2;
            Q2=makeQuery(id+"F7.opExtrude","SWEPT_EDGE",EDGE,{"disambiguationData":[OSD([sQuery(id+"F4.wireOp",EDGE,"E8.top"),sQuery(id+"F4.wireOp",EDGE,"E8.left")])]});
            var Q3;
            Q3=makeQuery(id+"F7.opExtrude","SWEPT_EDGE",EDGE,{"disambiguationData":[OSD([sQuery(id+"F4.wireOp",EDGE,"E5.top"),sQuery(id+"F4.wireOp",EDGE,"E5.right")])]});
            var Q4;
            Q4=makeQuery(id+"F7.opExtrude","SWEPT_EDGE",EDGE,{"disambiguationData":[OSD([sQuery(id+"F4.wireOp",EDGE,"E8.top"),sQuery(id+"F4.wireOp",EDGE,"E8.right")])]});
            var Q5;
            Q5=makeQuery(id+"F7.opExtrude","SWEPT_EDGE",EDGE,{"disambiguationData":[OSD([sQuery(id+"F4.wireOp",EDGE,"E5.top"),sQuery(id+"F4.wireOp",EDGE,"E5.left")])]});
            var Q6;
            Q6=makeQuery(id+"F7.opExtrude","SWEPT_EDGE",EDGE,{"disambiguationData":[OSD([sQuery(id+"F4.wireOp",EDGE,"E5.bottom"),sQuery(id+"F4.wireOp",EDGE,"E5.left")])]});
            var Q7;
            Q7=makeQuery(id+"F7.opExtrude","SWEPT_EDGE",EDGE,{"disambiguationData":[OSD([sQuery(id+"F4.wireOp",EDGE,"E5.bottom"),sQuery(id+"F4.wireOp",EDGE,"E5.right")])]});
            fillet(context, id + "F52", {"entities" : qUnion([Q0, Q1, Q2, Q3, Q4, Q5, Q6, Q7]), "radius" : 5.08 * mm, "tangentPropagation" : true, "allowEdgeOverflow" : false});
        }
    });
